# Revit family: VT.VAR00.G.07
name_source: partatom
category: Оборудование
units: mm (PartAtom-declared; Revit-internal decimal feet)

## family parameters
Всегда вертикально = Да
Заголовок OmniClass = Climate Control (HVAC)
На основе рабочей плоскости = Нет
Номер OmniClass = 23.75.00.00
Общий = Нет
При загрузке вырезать с полостями = Нет
Размер круглого соединителя = Использовать диаметр
Тип детали = Нормальный
Точка расчета площади = Нет

## types (1)
- VT.VAR00.G.07
    1.4 Описание = Климат-контроль установки и оборудование (HVAC)
    2.0 Описание = Клапаны
    Article Description = Hydraulic separator/pressure equalizer with temperature/pressure guage and automatic air vent valve for VARIMIX system
    Article Type = VAR 00
    BIMобъект категории = Другие
    BIMобъект основная категория = водопровод
    Discharge of responsability = BIM models made by I.V.A.R. S.p.A. are designed as an aid to design and they must be always verified by the end user. I.V.A.R. S.p.A. has no responsibility for any direct or indirect damages of any kind, deriving or resulting from the use of such files.
    EMCS Version = 3.0
    Family Version = Rev.00
    Produced in = Made in Italy
    Product Line = модуль быстрого монтажа VARIMIX гидравлический разделитель (гидрострелка)
    Revit Version = 2018
    URL = https://valtec.ru
    VALTEC = https://valtec.ru
    Вес нетто (кг) = 4,5
    Группа модели = VAR 00
    Группа товаров = VARIMIX
    Изготовитель = IVAR
    Инструкция по установке = https://valtec.ru
    Код категории BIMобъекта = водопроводным-другой
    Код основной категории BIMobject = водопровод
    Макс рабочая температура (°C) = 120 °C
    Макс рабочее давление (бар) = 10 бары
    Максимальная скорость потока (л/ч) = 4500
    Материал = Латунь - CB753S
    Материал основной = Латунь
    Номинальная высота = 0 мм
    Номинальная ширина = 0 мм
    Общий поток подачи гидравлики = 0.0 л/с
    Описание = Hydraulic separator/pressure equalizer with temperature/pressure guage and automatic air vent valve for VARIMIX system
    Описание OmniClass = HVAC Специальные продукты и оборудование
    Описание Конфигурации = Гидравлический сепаратор / выравниватель давления с датчиком температуры / давления и автоматическим вентиляционным клапаном для системы VARIMIX.
    Пенополистрирольная теплоизоляция = Да
    Полный гидравлический возвратный поток = 0.0 л/с
    Практическое руководство по использованию семьи = - Вы можете выбрать, где разместить обратное соединение.
Отметьте эту опцию в параметрах «Свойства модели - Прямое обратное соединение» или «Свойства модели - Угловое обратное соединение».
    Производитель = IVAR
    Размер соединения = G 1"1/4 F
    Страна изготовитель = Italy
